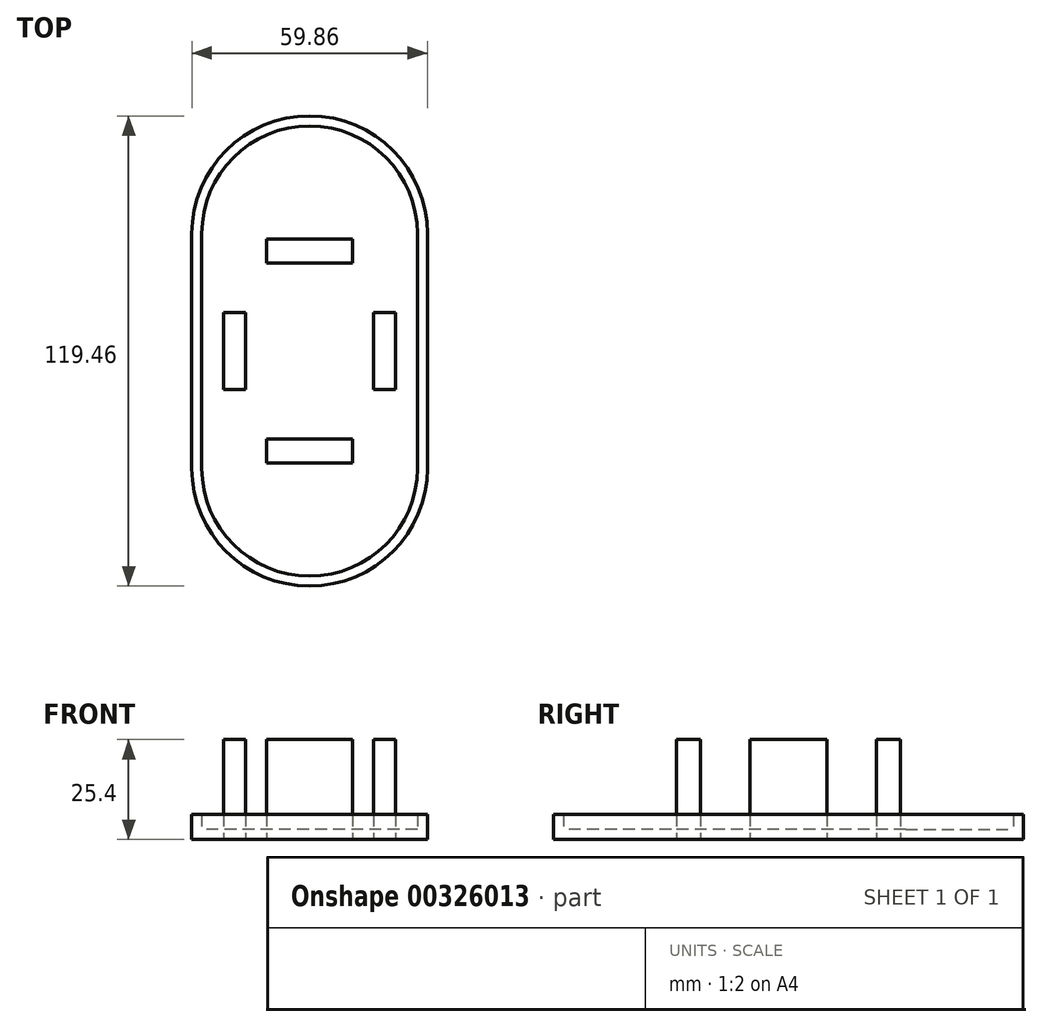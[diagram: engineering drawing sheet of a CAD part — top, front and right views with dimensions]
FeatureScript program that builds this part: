
annotation { "Feature Type Name" : "Feature", "Feature Type Description" : "" }
export const myFeature = defineFeature(function(context is Context, id is Id, definition is map)
    precondition{}
    {
        {
            var Q0;
            Q0=qCreatedBy(makeId("Top.planeOp"),FACE);
            var sketch = newSketch(context, id + "F0", { "sketchPlane" : qUnion([Q0])});
            skLineSegment(sketch, "E0.left", {"start": v(-29.93, 29.8) * mm, "end": v(-29.93, -29.8) * mm});
            skLineSegment(sketch, "E0.right", {"start": v(29.93, 29.8) * mm, "end": v(29.93, -29.8) * mm});
            skPoint(sketch, "E0.middle", {"position": v(0, 0) * mm});
            skArc(sketch, "E1", {"start": v(29.93, 29.8) * mm, "mid": v(0, 59.73) * mm, "end": v(-29.93, 29.8) * mm});
            skArc(sketch, "E2", {"start": v(-29.93, -29.8) * mm, "mid": v(0, -59.73) * mm, "end": v(29.93, -29.8) * mm});
            skLineSegment(sketch, "E3", {"start": v(0, 59.73) * mm, "end": v(0, -59.73) * mm, "construction": true});
            skLineSegment(sketch, "E4", {"start": v(-29.93, 29.8) * mm, "end": v(29.93, 29.8) * mm, "construction": true});
            skLineSegment(sketch, "E5", {"start": v(-29.93, -29.8) * mm, "end": v(29.93, -29.8) * mm, "construction": true});
            skLineSegment(sketch, "E6", {"start": v(0, 0) * mm, "end": v(29.93, 0) * mm, "construction": true});
            skPoint(sketch, "E7.end.orphan", {"position": v(-29.93, 0) * mm});
            skLineSegment(sketch, "E8", {"start": v(-29.93, 0) * mm, "end": v(0, 0) * mm, "construction": true});
            skSolve(sketch);
        }
        {
            var Q0;
            Q0=makeQuery(id+"F0.imprint","IMPRINT",FACE,{"disambiguationData":[TD([[makeQuery(id+"F0.imprint","IMPRINT",EDGE,{"derivedFrom":sQuery(id+"F0.wireOp",EDGE,"E0.left")}),1.0]])]});
            var sketch = newSketch(context, id + "F1", { "sketchPlane" : qUnion([Q0])});
            skLineSegment(sketch, "E9.bottom", {"start": v(-10.96, 28.42) * mm, "end": v(10.96, 28.42) * mm});
            skLineSegment(sketch, "E9.top", {"start": v(-10.96, 22.38) * mm, "end": v(10.96, 22.38) * mm});
            skLineSegment(sketch, "E9.left", {"start": v(-10.96, 28.42) * mm, "end": v(-10.96, 22.38) * mm});
            skLineSegment(sketch, "E9.right", {"start": v(10.96, 28.42) * mm, "end": v(10.96, 22.38) * mm});
            skPoint(sketch, "E9.middle", {"position": v(0, 25.4) * mm});
            skLineSegment(sketch, "E10.bottom", {"start": v(-10.96, -22.38) * mm, "end": v(10.96, -22.38) * mm});
            skLineSegment(sketch, "E10.top", {"start": v(-10.96, -28.42) * mm, "end": v(10.96, -28.42) * mm});
            skLineSegment(sketch, "E10.left", {"start": v(-10.96, -22.38) * mm, "end": v(-10.96, -28.42) * mm});
            skLineSegment(sketch, "E10.right", {"start": v(10.96, -22.38) * mm, "end": v(10.96, -28.42) * mm});
            skPoint(sketch, "E10.middle", {"position": v(0, -25.4) * mm});
            skLineSegment(sketch, "E11.bottom", {"start": v(-21.85, 9.76) * mm, "end": v(-16.25, 9.76) * mm});
            skLineSegment(sketch, "E11.top", {"start": v(-21.85, -9.76) * mm, "end": v(-16.25, -9.76) * mm});
            skLineSegment(sketch, "E11.left", {"start": v(-21.85, 9.76) * mm, "end": v(-21.85, -9.76) * mm});
            skLineSegment(sketch, "E11.right", {"start": v(-16.25, 9.76) * mm, "end": v(-16.25, -9.76) * mm});
            skPoint(sketch, "E11.middle", {"position": v(-19.05, 0) * mm});
            skLineSegment(sketch, "E12.bottom", {"start": v(16.25, 9.76) * mm, "end": v(21.85, 9.76) * mm});
            skLineSegment(sketch, "E12.top", {"start": v(16.25, -9.76) * mm, "end": v(21.85, -9.76) * mm});
            skLineSegment(sketch, "E12.left", {"start": v(16.25, 9.76) * mm, "end": v(16.25, -9.76) * mm});
            skLineSegment(sketch, "E12.right", {"start": v(21.85, 9.76) * mm, "end": v(21.85, -9.76) * mm});
            skPoint(sketch, "E12.middle", {"position": v(19.05, 0) * mm});
            skPoint(sketch, "E12.middle.positionSnap0", {"position": v(-21.85, 0) * mm});
            skPoint(sketch, "E12.centerSnap0", {"position": v(-21.85, 0) * mm});
            skSolve(sketch);
        }
        {
            var Q0;
            Q0 = qSketchRegion(id + "F1", true);
            extrude(context, id + "F2", {"entities" : qUnion([Q0]), "depth" : 25.4 * mm});
        }
        {
            var Q0;
            Q0 = qSketchRegion(id + "F0", true);
            extrude(context, id + "F3", {"entities" : qUnion([Q0]), "depth" : 6.35 * mm});
        }
        {
            var Q0;
            Q0=makeQuery(id+"F3.opExtrude","CAP_FACE",FACE,{"disambiguationData":[OSD([sQuery(id+"F0.wireOp",EDGE,"E0.left"),sQuery(id+"F0.wireOp",EDGE,"E0.right"),sQuery(id+"F0.wireOp",EDGE,"E1"),sQuery(id+"F0.wireOp",EDGE,"E2")])],"isStart":false});
            shell(context, id + "F4", {"entities" : qUnion([Q0]), "thickness" : 2.54 * mm});
        }
        {
            var Q0;
            Q0=qCreatedBy(makeId("Right.planeOp"),FACE);
            var sketch = newSketch(context, id + "F5", { "sketchPlane" : qUnion([Q0])});
            skLineSegment(sketch, "E13", {"start": v(28.6, 25.56) * mm, "end": v(37.14, 0) * mm});
            skSolve(sketch);
        }
    });
